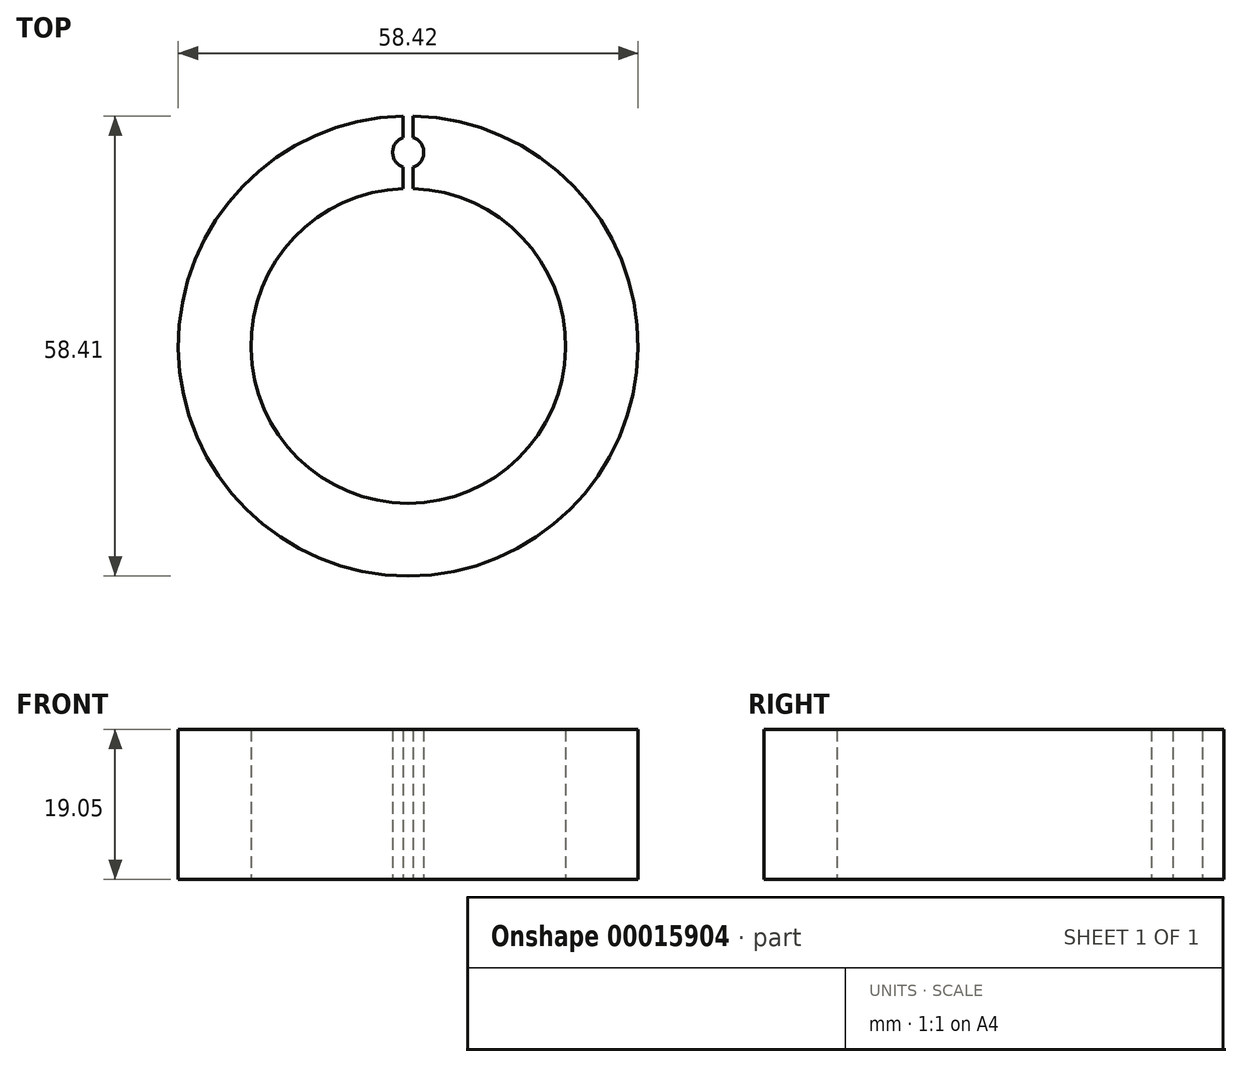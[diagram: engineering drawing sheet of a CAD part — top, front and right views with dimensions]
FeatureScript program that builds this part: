
annotation { "Feature Type Name" : "Feature", "Feature Type Description" : "" }
export const myFeature = defineFeature(function(context is Context, id is Id, definition is map)
    precondition{}
    {
        {
            var Q0;
            Q0=qCreatedBy(makeId("Top.planeOp"),FACE);
            var sketch = newSketch(context, id + "F0", { "sketchPlane" : qUnion([Q0])});
            skArc(sketch, "E0", {"start": v(-0.64, 29.2) * mm, "mid": v(0, -29.2) * mm, "end": v(0.64, 29.2) * mm});
            skArc(sketch, "E1", {"start": v(-0.63, 19.98) * mm, "mid": v(0, -19.99) * mm, "end": v(0.64, 19.98) * mm});
            skLineSegment(sketch, "E2", {"start": v(0, 29.21) * mm, "end": v(0, 19.99) * mm, "construction": true});
            skPoint(sketch, "E3.orphan", {"position": v(0, 33.1) * mm});
            skArc(sketch, "E4", {"start": v(0.64, 22.72) * mm, "mid": v(1.98, 24.6) * mm, "end": v(0.64, 26.48) * mm});
            skLineSegment(sketch, "E5", {"start": v(0.64, 19.98) * mm, "end": v(0.64, 29.2) * mm});
            skLineSegment(sketch, "E6.MirrorCS", {"start": v(-0.64, 19.98) * mm, "end": v(-0.64, 29.2) * mm});
            skPoint(sketch, "E7.orphan", {"position": v(0.64, 18.57) * mm});
            skPoint(sketch, "E8.orphan", {"position": v(-0.64, 18.57) * mm});
            skPoint(sketch, "E9.orphan", {"position": v(0.64, 30.3) * mm});
            skPoint(sketch, "E10.orphan", {"position": v(-0.64, 30.3) * mm});
            skArc(sketch, "E11.trimOffspring", {"start": v(-0.63, 26.48) * mm, "mid": v(-1.98, 24.6) * mm, "end": v(-0.63, 22.72) * mm});
            skSolve(sketch);
        }
        {
            var Q0;
            {var subQ2=sQuery(id+"F0.wireOp",EDGE,"E0");Q0=makeQuery(id+"F0.imprint","IMPRINT",FACE,{"disambiguationData":[TD([[makeQuery(id+"F0.imprint","IMPRINT",EDGE,{"derivedFrom":subQ2}),1.0]])]});}
            extrude(context, id + "F1", {"entities" : qUnion([Q0]), "depth" : 19.05 * mm});
        }
    });
